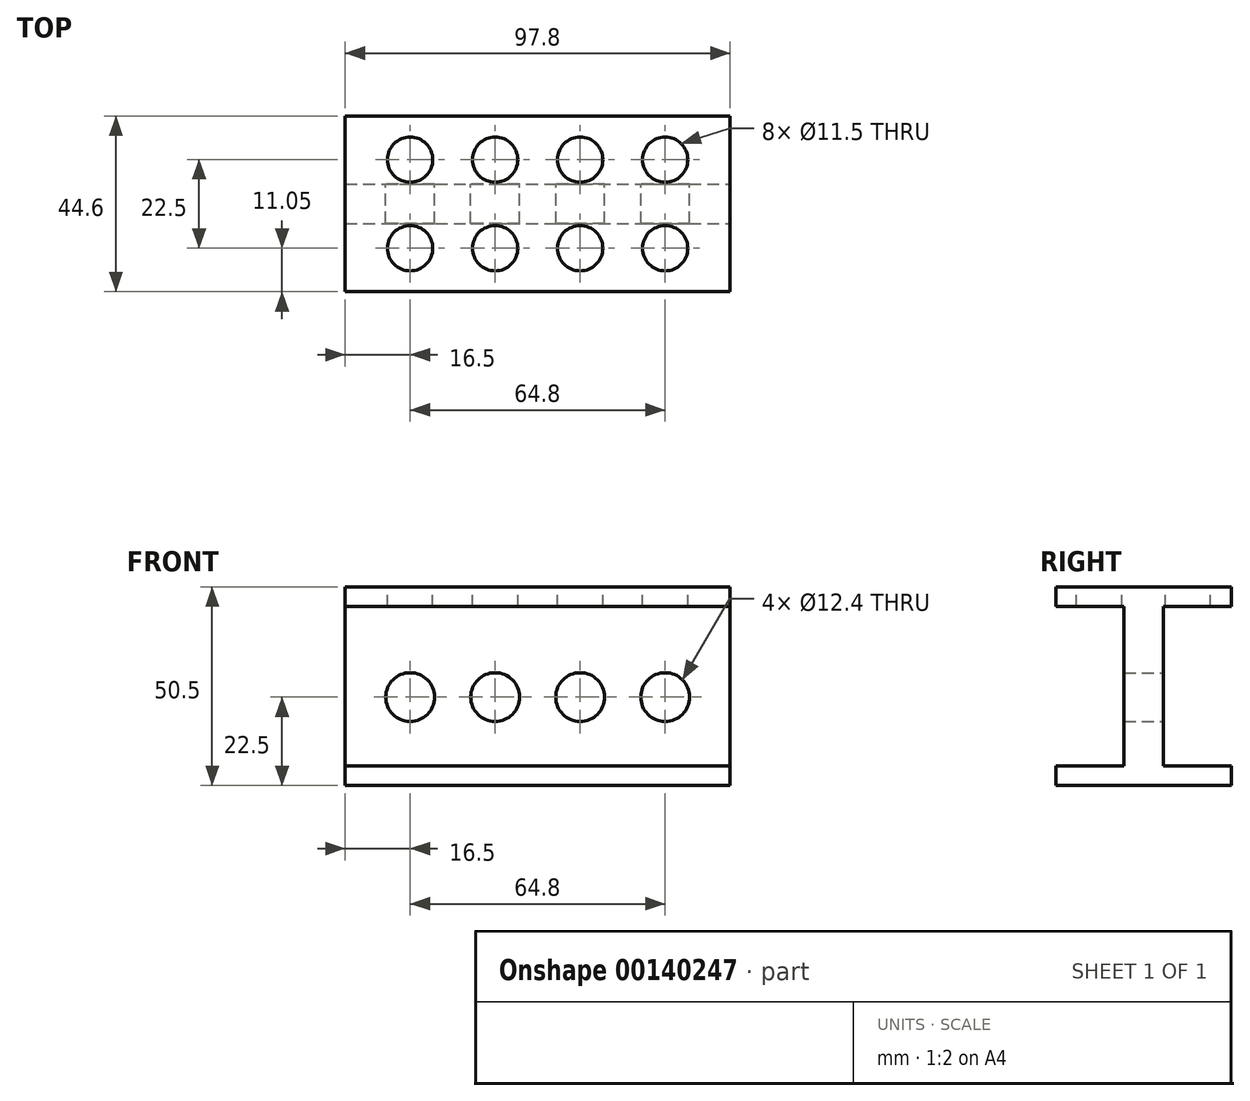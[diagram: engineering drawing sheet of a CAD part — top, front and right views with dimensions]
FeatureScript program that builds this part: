
annotation { "Feature Type Name" : "Feature", "Feature Type Description" : "" }
export const myFeature = defineFeature(function(context is Context, id is Id, definition is map)
    precondition{}
    {
        {
            var Q0;
            Q0=qCreatedBy(makeId("Front.planeOp"),FACE);
            var sketch = newSketch(context, id + "F0", { "sketchPlane" : qUnion([Q0])});
            skLineSegment(sketch, "E0.bottom", {"start": v(38.1, 25.25) * mm, "end": v(-38.1, 25.25) * mm});
            skLineSegment(sketch, "E0.top", {"start": v(38.1, -25.25) * mm, "end": v(-38.1, -25.25) * mm});
            skLineSegment(sketch, "E0.right", {"start": v(-38.1, 25.25) * mm, "end": v(-38.1, -25.25) * mm});
            skPoint(sketch, "E0.middle", {"position": v(0, 0) * mm});
            skLineSegment(sketch, "E1.0", {"start": v(38.1, -20.25) * mm, "end": v(-38.1, -20.25) * mm});
            skLineSegment(sketch, "E2.0", {"start": v(38.1, 20.25) * mm, "end": v(-38.1, 20.25) * mm});
            skLineSegment(sketch, "E3.0", {"start": v(38.1, -2.75) * mm, "end": v(-38.1, -2.75) * mm});
            skLineSegment(sketch, "E4", {"start": v(0, -2.75) * mm, "end": v(21.6, -2.75) * mm});
            skCircle(sketch, "E5", {"center": v(0, -2.75) * mm, "radius": 6.2 * mm});
            skCircle(sketch, "E6", {"center": v(21.6, -2.75) * mm, "radius": 6.2 * mm});
            skCircle(sketch, "E7.MirrorC", {"center": v(-21.6, -2.75) * mm, "radius": 6.2 * mm});
            skLineSegment(sketch, "E8", {"start": v(21.6, -2.75) * mm, "end": v(43.2, -2.75) * mm});
            skLineSegment(sketch, "E9", {"start": v(43.2, -2.75) * mm, "end": v(59.7, -2.75) * mm});
            skLineSegment(sketch, "E10.bottom", {"start": v(38.1, 25.25) * mm, "end": v(59.7, 25.25) * mm});
            skLineSegment(sketch, "E10.top", {"start": v(38.1, -2.75) * mm, "end": v(59.7, -2.75) * mm});
            skLineSegment(sketch, "E10.right", {"start": v(59.7, 25.25) * mm, "end": v(59.7, -2.75) * mm});
            skLineSegment(sketch, "E11.bottom", {"start": v(59.7, -2.75) * mm, "end": v(38.1, -2.75) * mm});
            skLineSegment(sketch, "E11.top", {"start": v(59.7, -25.25) * mm, "end": v(38.1, -25.25) * mm});
            skLineSegment(sketch, "E11.left", {"start": v(59.7, -2.75) * mm, "end": v(59.7, -25.25) * mm});
            skLineSegment(sketch, "E12", {"start": v(38.1, 20.25) * mm, "end": v(59.7, 20.25) * mm});
            skLineSegment(sketch, "E13", {"start": v(38.1, -20.25) * mm, "end": v(59.7, -20.25) * mm});
            skCircle(sketch, "E14", {"center": v(43.2, -2.75) * mm, "radius": 6.2 * mm});
            skSolve(sketch);
        }
        {
            var Q0;
            {var subQ0=sQuery(id+"F0.wireOp",EDGE,"E0.bottom");Q0=makeQuery(id+"F0.imprint","IMPRINT",FACE,{"disambiguationData":[TD([[makeQuery(id+"F0.imprint","IMPRINT",EDGE,{"derivedFrom":subQ0}),1.0]])]});}
            extrude(context, id + "F1", {"entities" : qUnion([Q0]), "endBound" : BoundingType.SYMMETRIC, "depth" : 44.6 * mm});
        }
        {
            var Q0;
            Q0=makeQuery(id+"F1.opExtrude","SWEPT_FACE",FACE,{"disambiguationData":[OSD([sQuery(id+"F0.wireOp",EDGE,"E0.bottom")])]});
            var sketch = newSketch(context, id + "F2", { "sketchPlane" : qUnion([Q0])});
            skLineSegment(sketch, "E15", {"start": v(0, 0) * mm, "end": v(0, 10.25) * mm});
            skCircle(sketch, "E16", {"center": v(0, 10.25) * mm, "radius": 5.45 * mm});
            skLineSegment(sketch, "E17", {"start": v(0, 10.25) * mm, "end": v(21.6, 10.25) * mm});
            skLineSegment(sketch, "E18", {"start": v(0, 10.25) * mm, "end": v(-21.6, 10.25) * mm});
            skLineSegment(sketch, "E19", {"start": v(0, 0) * mm, "end": v(0, -10.25) * mm});
            skLineSegment(sketch, "E20", {"start": v(0, -10.25) * mm, "end": v(-21.6, -10.25) * mm});
            skLineSegment(sketch, "E21", {"start": v(0, -10.25) * mm, "end": v(21.6, -10.25) * mm});
            skCircle(sketch, "E22", {"center": v(21.6, -10.25) * mm, "radius": 5.45 * mm});
            skCircle(sketch, "E23", {"center": v(21.6, 10.25) * mm, "radius": 5.45 * mm});
            skCircle(sketch, "E24", {"center": v(0, -10.25) * mm, "radius": 5.45 * mm});
            skCircle(sketch, "E25", {"center": v(-21.6, 10.25) * mm, "radius": 5.45 * mm});
            skCircle(sketch, "E26", {"center": v(-21.6, -10.25) * mm, "radius": 5.45 * mm});
            skLineSegment(sketch, "E27.0", {"start": v(0, 11.25) * mm, "end": v(-21.6, 11.25) * mm});
            skLineSegment(sketch, "E27.1", {"start": v(0, 11.25) * mm, "end": v(21.6, 11.25) * mm});
            skLineSegment(sketch, "E28.0", {"start": v(0, -11.25) * mm, "end": v(21.6, -11.25) * mm});
            skLineSegment(sketch, "E28.1", {"start": v(0, -11.25) * mm, "end": v(-21.6, -11.25) * mm});
            skLineSegment(sketch, "E29", {"start": v(21.6, -11.25) * mm, "end": v(43.2, -11.25) * mm});
            skLineSegment(sketch, "E30", {"start": v(21.6, 11.25) * mm, "end": v(43.2, 11.25) * mm});
            skSolve(sketch);
        }
        {
            var Q0;
            Q0=sQuery(id+"F2.wireOp",VERTEX,"E27.0.end");
            var Q1;
            Q1=sQuery(id+"F2.wireOp",VERTEX,"E27.1.start");
            var Q2;
            Q2=sQuery(id+"F2.wireOp",VERTEX,"E27.1.end");
            var Q3;
            Q3=sQuery(id+"F2.wireOp",VERTEX,"E28.0.end");
            var Q4;
            Q4=sQuery(id+"F2.wireOp",VERTEX,"E28.0.start");
            var Q5;
            Q5=sQuery(id+"F2.wireOp",VERTEX,"E28.1.end");
            var Q6;
            Q6=sQuery(id+"F2.wireOp",VERTEX,"E30.end");
            var Q7;
            Q7=sQuery(id+"F2.wireOp",VERTEX,"E29.end");
            var Q8;
            Q8=makeQuery(id+"F1.opExtrude","SWEPT_BODY",BODY,{"disambiguationData":[OSD([sQuery(id+"F0.wireOp",EDGE,"E0.bottom"),sQuery(id+"F0.wireOp",EDGE,"E0.left"),sQuery(id+"F0.wireOp",EDGE,"E0.right"),sQuery(id+"F0.wireOp",EDGE,"E2.0")])]});
            hole(context, id + "F3", {"style" : HoleStyle.SIMPLE, "endStyle" : HoleEndStyle.THROUGH, "holeDiameter" : 11.5 * mm, "locations" : qUnion([Q0, Q1, Q2, Q3, Q4, Q5, Q6, Q7]), "scope" : qUnion([Q8]), "isTappedThrough" : true});
        }
        {
            var Q0;
            {var subQ5=sQuery(id+"F0.wireOp",EDGE,"E2.0");Q0=makeQuery(id+"F0.imprint","IMPRINT",FACE,{"disambiguationData":[TD([[makeQuery(id+"F0.imprint","IMPRINT",EDGE,{"derivedFrom":subQ5}),1.0]])]});}
            var Q1;
            {var subQ5=sQuery(id+"F0.wireOp",EDGE,"E1.0");Q1=makeQuery(id+"F0.imprint","IMPRINT",FACE,{"disambiguationData":[TD([[makeQuery(id+"F0.imprint","IMPRINT",EDGE,{"derivedFrom":subQ5}),-1.0]])]});}
            extrude(context, id + "F4", {"entities" : qUnion([Q0, Q1]), "operationType" : NewBodyOperationType.ADD, "endBound" : BoundingType.SYMMETRIC, "depth" : 10 * mm});
        }
        {
            var Q0;
            {var subQ0=sQuery(id+"F0.wireOp",EDGE,"E0.top");Q0=makeQuery(id+"F0.imprint","IMPRINT",FACE,{"disambiguationData":[TD([[makeQuery(id+"F0.imprint","IMPRINT",EDGE,{"derivedFrom":subQ0}),-1.0]])]});}
            extrude(context, id + "F5", {"entities" : qUnion([Q0]), "operationType" : NewBodyOperationType.ADD, "endBound" : BoundingType.SYMMETRIC, "depth" : 44.6 * mm});
        }
    });
